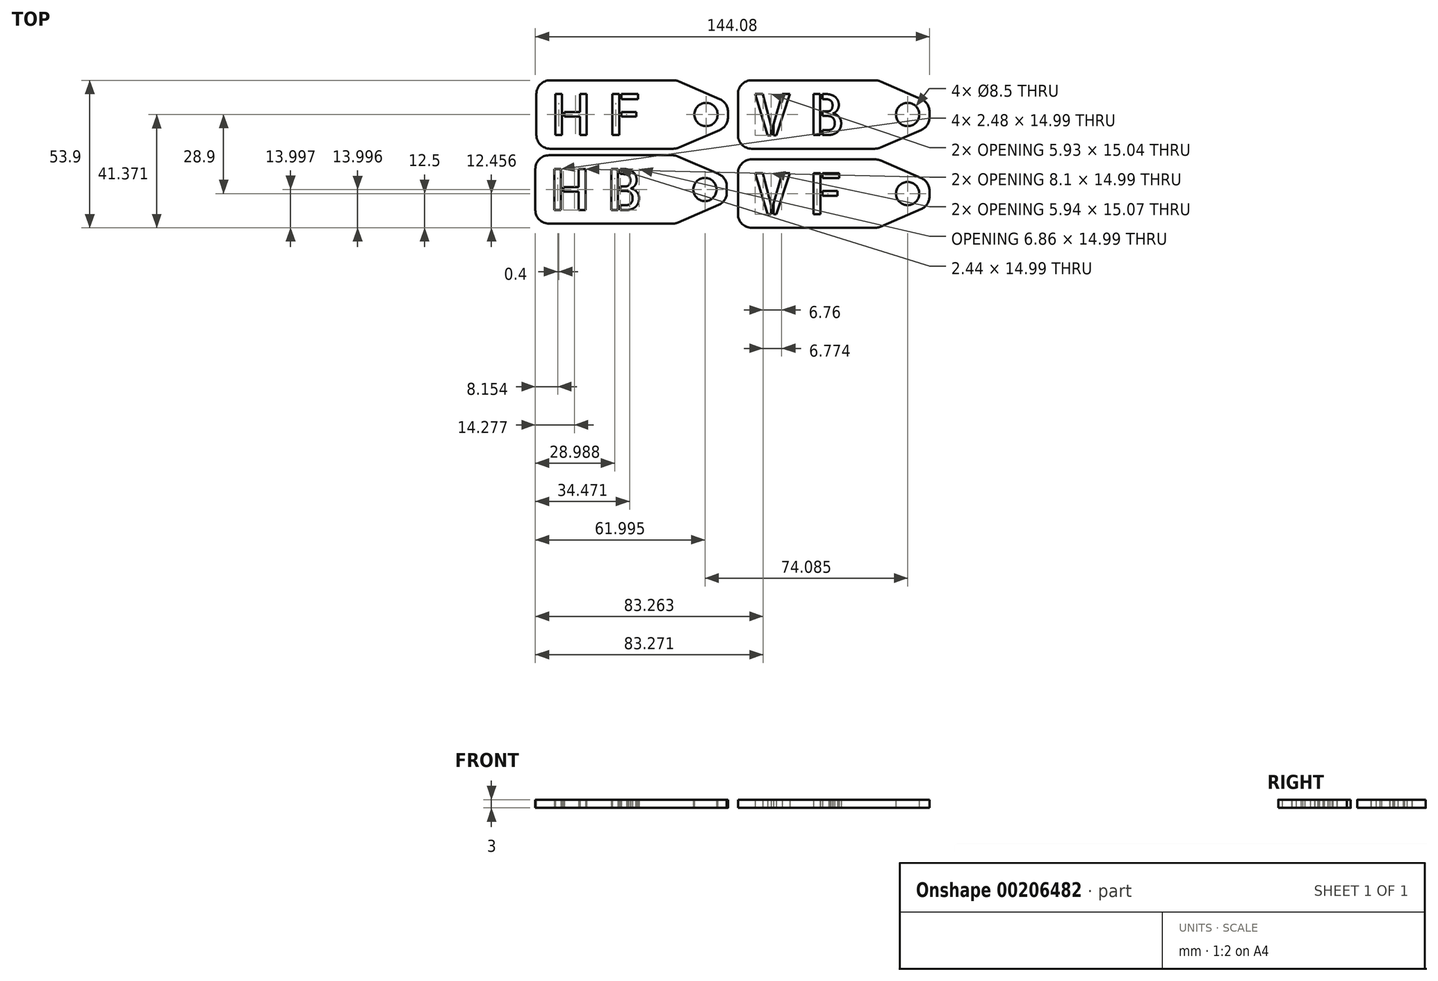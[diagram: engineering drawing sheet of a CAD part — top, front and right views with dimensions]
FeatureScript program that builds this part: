
annotation { "Feature Type Name" : "Feature", "Feature Type Description" : "" }
export const myFeature = defineFeature(function(context is Context, id is Id, definition is map)
    precondition{}
    {
        {
            var Q0;
            Q0=qCreatedBy(makeId("Top.planeOp"),FACE);
            var sketch = newSketch(context, id + "F0", { "sketchPlane" : qUnion([Q0])});
            skLineSegment(sketch, "E0.bottom", {"start": v(5, 0) * mm, "end": v(50.12, 0) * mm});
            skLineSegment(sketch, "E0.top", {"start": v(5, 25) * mm, "end": v(50.12, 25) * mm});
            skLineSegment(sketch, "E0.left", {"start": v(0, 5) * mm, "end": v(0, 20) * mm});
            skLineSegment(sketch, "E0.right", {"start": v(70, 11.44) * mm, "end": v(70, 13.56) * mm});
            skCircle(sketch, "E1", {"center": v(62, 12.5) * mm, "radius": 4.25 * mm});
            skPoint(sketch, "E1.centerSnap0", {"position": v(70, 12.5) * mm});
            skLineSegment(sketch, "E2", {"start": v(52.1, 24.59) * mm, "end": v(66.99, 18.15) * mm});
            skLineSegment(sketch, "E3", {"start": v(70, 12.5) * mm, "end": v(36.07, 12.5) * mm, "construction": true});
            skLineSegment(sketch, "E4.MirrorCS", {"start": v(52.1, 0.41) * mm, "end": v(66.99, 6.85) * mm});
            skPoint(sketch, "E5.orphan", {"position": v(70, 25) * mm});
            skPoint(sketch, "E6.orphan", {"position": v(70, 0) * mm});
            skPoint(sketch, "E7.visualSharp", {"position": v(70, 16.85) * mm});
            skArc(sketch, "E7.filletArc", {"start": v(70, 13.56) * mm, "mid": v(69.18, 16.3) * mm, "end": v(66.99, 18.15) * mm});
            skPoint(sketch, "E8.visualSharp", {"position": v(70, 8.15) * mm});
            skArc(sketch, "E8.filletArc", {"start": v(66.99, 6.85) * mm, "mid": v(69.18, 8.7) * mm, "end": v(70, 11.44) * mm});
            skPoint(sketch, "E9.visualSharp", {"position": v(51.16, 25) * mm});
            skArc(sketch, "E9.filletArc", {"start": v(52.1, 24.59) * mm, "mid": v(51.13, 24.9) * mm, "end": v(50.12, 25) * mm});
            skPoint(sketch, "E10.visualSharp", {"position": v(51.16, 0) * mm});
            skArc(sketch, "E10.filletArc", {"start": v(50.12, 0) * mm, "mid": v(51.13, 0.1) * mm, "end": v(52.1, 0.41) * mm});
            skPoint(sketch, "E11.visualSharp", {"position": v(0, 25) * mm});
            skArc(sketch, "E11.filletArc", {"start": v(5, 25) * mm, "mid": v(1.46, 23.54) * mm, "end": v(0, 20) * mm});
            skPoint(sketch, "E12.visualSharp", {"position": v(0, 0) * mm});
            skArc(sketch, "E12.filletArc", {"start": v(0, 5) * mm, "mid": v(1.46, 1.46) * mm, "end": v(5, 0) * mm});
            skText(sketch, "E13", { "text": "V B", "fontName": "AllertaStencil-Regular.ttf"});
            const initialGuessF0  = {"E13": [0.005, 0.00503, 1, 0, 0.01497]};
            skSetInitialGuess(sketch, initialGuessF0);
            skSolve(sketch);
        }
        {
            var Q0;
            Q0=qCreatedBy(makeId("Top.planeOp"),FACE);
            var sketch = newSketch(context, id + "F1", { "sketchPlane" : qUnion([Q0])});
            skLineSegment(sketch, "E14.bottom", {"start": v(5, -28.9) * mm, "end": v(50.12, -28.9) * mm});
            skLineSegment(sketch, "E14.top", {"start": v(5, -3.9) * mm, "end": v(50.12, -3.9) * mm});
            skLineSegment(sketch, "E14.left", {"start": v(0, -23.9) * mm, "end": v(0, -8.9) * mm});
            skLineSegment(sketch, "E14.right", {"start": v(70, -17.46) * mm, "end": v(70, -15.34) * mm});
            skCircle(sketch, "E15", {"center": v(62, -16.4) * mm, "radius": 4.25 * mm});
            skPoint(sketch, "E15.centerSnap0", {"position": v(70, -16.4) * mm});
            skLineSegment(sketch, "E16", {"start": v(52.1, -4.31) * mm, "end": v(66.99, -10.75) * mm});
            skLineSegment(sketch, "E17", {"start": v(70, -16.4) * mm, "end": v(36.07, -16.4) * mm, "construction": true});
            skLineSegment(sketch, "E18.MirrorCS", {"start": v(52.1, -28.49) * mm, "end": v(66.99, -22.05) * mm});
            skPoint(sketch, "E19.orphan", {"position": v(70, -3.9) * mm});
            skPoint(sketch, "E20.orphan", {"position": v(70, -28.9) * mm});
            skPoint(sketch, "E21.visualSharp", {"position": v(70, -12.05) * mm});
            skArc(sketch, "E21.filletArc", {"start": v(70, -15.34) * mm, "mid": v(69.18, -12.6) * mm, "end": v(66.99, -10.75) * mm});
            skPoint(sketch, "E22.visualSharp", {"position": v(70, -20.75) * mm});
            skArc(sketch, "E22.filletArc", {"start": v(66.99, -22.05) * mm, "mid": v(69.18, -20.2) * mm, "end": v(70, -17.46) * mm});
            skPoint(sketch, "E23.visualSharp", {"position": v(51.16, -3.9) * mm});
            skArc(sketch, "E23.filletArc", {"start": v(52.1, -4.31) * mm, "mid": v(51.13, -4) * mm, "end": v(50.12, -3.9) * mm});
            skPoint(sketch, "E24.visualSharp", {"position": v(51.16, -28.9) * mm});
            skArc(sketch, "E24.filletArc", {"start": v(50.12, -28.9) * mm, "mid": v(51.13, -28.8) * mm, "end": v(52.1, -28.49) * mm});
            skPoint(sketch, "E25.visualSharp", {"position": v(0, -3.9) * mm});
            skArc(sketch, "E25.filletArc", {"start": v(5, -3.9) * mm, "mid": v(1.46, -5.36) * mm, "end": v(0, -8.9) * mm});
            skPoint(sketch, "E26.visualSharp", {"position": v(0, -28.9) * mm});
            skArc(sketch, "E26.filletArc", {"start": v(0, -23.9) * mm, "mid": v(1.46, -27.44) * mm, "end": v(5, -28.9) * mm});
            skText(sketch, "E27", { "text": "V F", "fontName": "AllertaStencil-Regular.ttf"});
            const initialGuessF1  = {"E27": [0.005, -0.0239, 1, 0, 0.015]};
            skSetInitialGuess(sketch, initialGuessF1);
            skSolve(sketch);
        }
        {
            var Q0;
            Q0=qCreatedBy(makeId("Top.planeOp"),FACE);
            var sketch = newSketch(context, id + "F2", { "sketchPlane" : qUnion([Q0])});
            skLineSegment(sketch, "E28.bottom", {"start": v(-68.68, 0) * mm, "end": v(-23.56, 0) * mm});
            skLineSegment(sketch, "E28.top", {"start": v(-68.68, 25) * mm, "end": v(-23.56, 25) * mm});
            skLineSegment(sketch, "E28.left", {"start": v(-73.68, 5) * mm, "end": v(-73.68, 20) * mm});
            skLineSegment(sketch, "E28.right", {"start": v(-3.68, 11.44) * mm, "end": v(-3.68, 13.56) * mm});
            skCircle(sketch, "E29", {"center": v(-11.68, 12.5) * mm, "radius": 4.25 * mm});
            skPoint(sketch, "E29.centerSnap0", {"position": v(-3.68, 12.5) * mm});
            skLineSegment(sketch, "E30", {"start": v(-21.58, 24.59) * mm, "end": v(-6.7, 18.15) * mm});
            skLineSegment(sketch, "E31", {"start": v(-3.68, 12.5) * mm, "end": v(-37.61, 12.5) * mm, "construction": true});
            skLineSegment(sketch, "E32.MirrorCS", {"start": v(-21.58, 0.41) * mm, "end": v(-6.7, 6.85) * mm});
            skPoint(sketch, "E33.orphan", {"position": v(-3.68, 25) * mm});
            skPoint(sketch, "E34.orphan", {"position": v(-3.68, 0) * mm});
            skPoint(sketch, "E35.visualSharp", {"position": v(-3.68, 16.85) * mm});
            skArc(sketch, "E35.filletArc", {"start": v(-3.68, 13.56) * mm, "mid": v(-4.5, 16.3) * mm, "end": v(-6.7, 18.15) * mm});
            skPoint(sketch, "E36.visualSharp", {"position": v(-3.68, 8.15) * mm});
            skArc(sketch, "E36.filletArc", {"start": v(-6.7, 6.85) * mm, "mid": v(-4.5, 8.7) * mm, "end": v(-3.68, 11.44) * mm});
            skPoint(sketch, "E37.visualSharp", {"position": v(-22.53, 25) * mm});
            skArc(sketch, "E37.filletArc", {"start": v(-21.58, 24.59) * mm, "mid": v(-22.55, 24.9) * mm, "end": v(-23.56, 25) * mm});
            skPoint(sketch, "E38.visualSharp", {"position": v(-22.53, 0) * mm});
            skArc(sketch, "E38.filletArc", {"start": v(-23.56, 0) * mm, "mid": v(-22.55, 0.1) * mm, "end": v(-21.58, 0.41) * mm});
            skPoint(sketch, "E39.visualSharp", {"position": v(-73.68, 25) * mm});
            skArc(sketch, "E39.filletArc", {"start": v(-68.68, 25) * mm, "mid": v(-72.22, 23.54) * mm, "end": v(-73.68, 20) * mm});
            skPoint(sketch, "E40.visualSharp", {"position": v(-73.68, 0) * mm});
            skArc(sketch, "E40.filletArc", {"start": v(-73.68, 5) * mm, "mid": v(-72.22, 1.46) * mm, "end": v(-68.68, 0) * mm});
            skText(sketch, "E41", { "text": "H F", "fontName": "AllertaStencil-Regular.ttf"});
            const initialGuessF2  = {"E41": [-0.06868, 0.005, 1, 0, 0.015]};
            skSetInitialGuess(sketch, initialGuessF2);
            skSolve(sketch);
        }
        {
            var Q0;
            Q0=qCreatedBy(makeId("Top.planeOp"),FACE);
            var sketch = newSketch(context, id + "F3", { "sketchPlane" : qUnion([Q0])});
            skLineSegment(sketch, "E42.bottom", {"start": v(-69.08, -27.4) * mm, "end": v(-23.96, -27.4) * mm});
            skLineSegment(sketch, "E42.top", {"start": v(-69.08, -2.4) * mm, "end": v(-23.96, -2.4) * mm});
            skLineSegment(sketch, "E42.left", {"start": v(-74.08, -22.4) * mm, "end": v(-74.08, -7.4) * mm});
            skLineSegment(sketch, "E42.right", {"start": v(-4.08, -15.96) * mm, "end": v(-4.08, -13.84) * mm});
            skCircle(sketch, "E43", {"center": v(-12.08, -14.9) * mm, "radius": 4.25 * mm});
            skPoint(sketch, "E43.centerSnap0", {"position": v(-4.08, -14.9) * mm});
            skLineSegment(sketch, "E44", {"start": v(-21.98, -2.81) * mm, "end": v(-7.1, -9.25) * mm});
            skLineSegment(sketch, "E45", {"start": v(-4.08, -14.9) * mm, "end": v(-38.01, -14.9) * mm, "construction": true});
            skLineSegment(sketch, "E46.MirrorCS", {"start": v(-21.98, -26.99) * mm, "end": v(-7.1, -20.55) * mm});
            skPoint(sketch, "E47.orphan", {"position": v(-4.08, -2.4) * mm});
            skPoint(sketch, "E48.orphan", {"position": v(-4.08, -27.4) * mm});
            skPoint(sketch, "E49.visualSharp", {"position": v(-4.08, -10.55) * mm});
            skArc(sketch, "E49.filletArc", {"start": v(-4.08, -13.84) * mm, "mid": v(-4.9, -11.1) * mm, "end": v(-7.1, -9.25) * mm});
            skPoint(sketch, "E50.visualSharp", {"position": v(-4.08, -19.25) * mm});
            skArc(sketch, "E50.filletArc", {"start": v(-7.1, -20.55) * mm, "mid": v(-4.9, -18.7) * mm, "end": v(-4.08, -15.96) * mm});
            skPoint(sketch, "E51.visualSharp", {"position": v(-22.93, -2.4) * mm});
            skArc(sketch, "E51.filletArc", {"start": v(-21.98, -2.81) * mm, "mid": v(-22.95, -2.5) * mm, "end": v(-23.96, -2.4) * mm});
            skPoint(sketch, "E52.visualSharp", {"position": v(-22.93, -27.4) * mm});
            skArc(sketch, "E52.filletArc", {"start": v(-23.96, -27.4) * mm, "mid": v(-22.95, -27.3) * mm, "end": v(-21.98, -26.99) * mm});
            skPoint(sketch, "E53.visualSharp", {"position": v(-74.08, -2.4) * mm});
            skArc(sketch, "E53.filletArc", {"start": v(-69.08, -2.4) * mm, "mid": v(-72.62, -3.86) * mm, "end": v(-74.08, -7.4) * mm});
            skPoint(sketch, "E54.visualSharp", {"position": v(-74.08, -27.4) * mm});
            skArc(sketch, "E54.filletArc", {"start": v(-74.08, -22.4) * mm, "mid": v(-72.62, -25.94) * mm, "end": v(-69.08, -27.4) * mm});
            skText(sketch, "E55", { "text": "H B", "fontName": "AllertaStencil-Regular.ttf"});
            const initialGuessF3  = {"E55": [-0.06908, -0.0224, 1, 0, 0.015]};
            skSetInitialGuess(sketch, initialGuessF3);
            skSolve(sketch);
        }
        {
            var Q0;
            Q0 = qSketchRegion(id + "F0", true);
            extrude(context, id + "F4", {"entities" : qUnion([Q0]), "depth" : 3 * mm, "offsetDistance" : 25 * mm});
        }
        {
            var Q0;
            Q0 = qSketchRegion(id + "F1", true);
            extrude(context, id + "F5", {"entities" : qUnion([Q0]), "depth" : 3 * mm, "offsetDistance" : 25 * mm});
        }
        {
            var Q0;
            Q0 = qSketchRegion(id + "F2", true);
            extrude(context, id + "F6", {"entities" : qUnion([Q0]), "depth" : 3 * mm, "offsetDistance" : 25 * mm});
        }
        {
            var Q0;
            Q0 = qSketchRegion(id + "F3", true);
            extrude(context, id + "F7", {"entities" : qUnion([Q0]), "depth" : 3 * mm, "offsetDistance" : 25 * mm});
        }
    });
